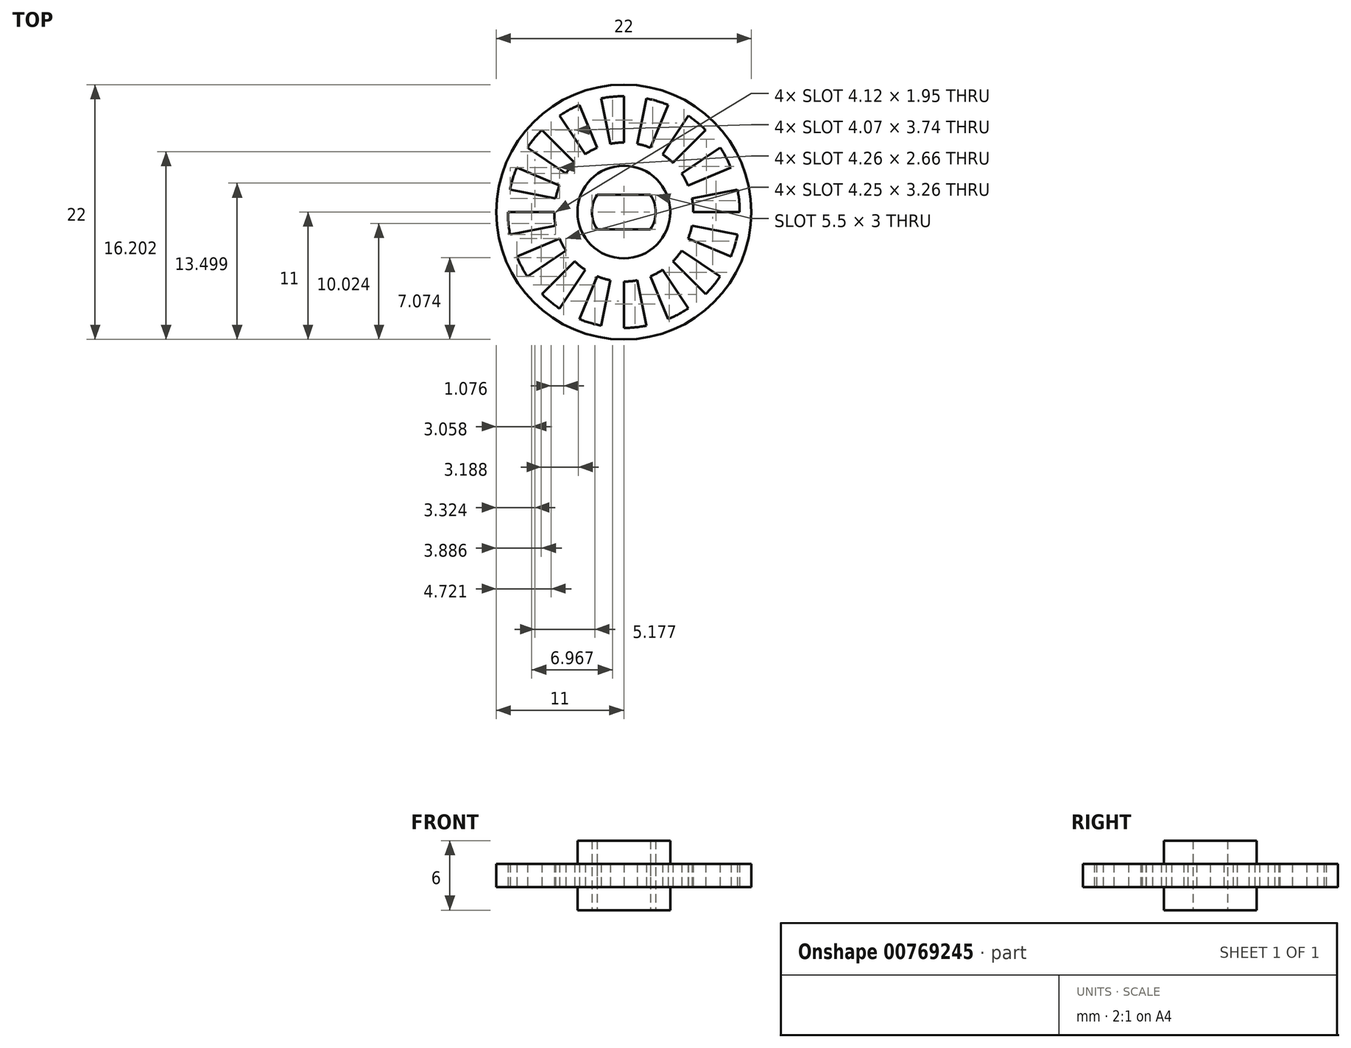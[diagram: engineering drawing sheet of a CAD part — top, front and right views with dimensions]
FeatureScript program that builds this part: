
annotation { "Feature Type Name" : "Feature", "Feature Type Description" : "" }
export const myFeature = defineFeature(function(context is Context, id is Id, definition is map)
    precondition{}
    {
        {
            var Q0;
            Q0=qCreatedBy(makeId("Top.planeOp"),FACE);
            var sketch = newSketch(context, id + "F0", { "sketchPlane" : qUnion([Q0])});
            skCircle(sketch, "E0", {"center": v(0, 0) * mm, "radius": 11 * mm});
            skArc(sketch, "E1", {"start": v(0, -10) * mm, "mid": v(0.98, -9.95) * mm, "end": v(1.95, -9.8) * mm});
            skArc(sketch, "E2", {"start": v(0, -6) * mm, "mid": v(0.59, -5.97) * mm, "end": v(1.17, -5.88) * mm});
            skLineSegment(sketch, "E3", {"start": v(0, -6) * mm, "end": v(0, -10) * mm});
            skLineSegment(sketch, "E4.1.0", {"start": v(1.17, -5.88) * mm, "end": v(1.95, -9.8) * mm});
            skLineSegment(sketch, "E4.2.0", {"start": v(2.3, -5.54) * mm, "end": v(3.83, -9.24) * mm});
            skLineSegment(sketch, "E4.3.0", {"start": v(3.33, -4.99) * mm, "end": v(5.56, -8.31) * mm});
            skLineSegment(sketch, "E4.4.0", {"start": v(4.24, -4.24) * mm, "end": v(7.07, -7.07) * mm});
            skLineSegment(sketch, "E4.5.0", {"start": v(4.99, -3.33) * mm, "end": v(8.31, -5.56) * mm});
            skLineSegment(sketch, "E4.6.0", {"start": v(5.54, -2.3) * mm, "end": v(9.24, -3.83) * mm});
            skLineSegment(sketch, "E4.7.0", {"start": v(5.88, -1.17) * mm, "end": v(9.8, -1.95) * mm});
            skLineSegment(sketch, "E4.8.0", {"start": v(6, 0) * mm, "end": v(10, 0) * mm});
            skLineSegment(sketch, "E4.9.0", {"start": v(5.88, 1.17) * mm, "end": v(9.8, 1.95) * mm});
            skLineSegment(sketch, "E4.10.0", {"start": v(5.54, 2.3) * mm, "end": v(9.24, 3.83) * mm});
            skLineSegment(sketch, "E4.11.0", {"start": v(4.99, 3.33) * mm, "end": v(8.31, 5.56) * mm});
            skLineSegment(sketch, "E4.12.0", {"start": v(4.24, 4.24) * mm, "end": v(7.07, 7.07) * mm});
            skLineSegment(sketch, "E4.13.0", {"start": v(3.33, 4.99) * mm, "end": v(5.56, 8.31) * mm});
            skLineSegment(sketch, "E4.14.0", {"start": v(2.3, 5.54) * mm, "end": v(3.83, 9.24) * mm});
            skLineSegment(sketch, "E4.15.0", {"start": v(1.17, 5.88) * mm, "end": v(1.95, 9.8) * mm});
            skLineSegment(sketch, "E4.16.0", {"start": v(0, 6) * mm, "end": v(0, 10) * mm});
            skLineSegment(sketch, "E4.17.0", {"start": v(-1.17, 5.88) * mm, "end": v(-1.95, 9.8) * mm});
            skLineSegment(sketch, "E4.18.0", {"start": v(-2.3, 5.54) * mm, "end": v(-3.83, 9.24) * mm});
            skLineSegment(sketch, "E4.19.0", {"start": v(-3.33, 4.99) * mm, "end": v(-5.56, 8.31) * mm});
            skLineSegment(sketch, "E4.20.0", {"start": v(-4.24, 4.24) * mm, "end": v(-7.07, 7.07) * mm});
            skLineSegment(sketch, "E4.21.0", {"start": v(-4.99, 3.33) * mm, "end": v(-8.31, 5.56) * mm});
            skLineSegment(sketch, "E4.22.0", {"start": v(-5.54, 2.3) * mm, "end": v(-9.24, 3.83) * mm});
            skLineSegment(sketch, "E4.23.0", {"start": v(-5.88, 1.17) * mm, "end": v(-9.8, 1.95) * mm});
            skLineSegment(sketch, "E4.24.0", {"start": v(-6, 0) * mm, "end": v(-10, 0) * mm});
            skLineSegment(sketch, "E4.25.0", {"start": v(-5.88, -1.17) * mm, "end": v(-9.8, -1.95) * mm});
            skLineSegment(sketch, "E4.26.0", {"start": v(-5.54, -2.3) * mm, "end": v(-9.24, -3.83) * mm});
            skLineSegment(sketch, "E4.27.0", {"start": v(-4.99, -3.33) * mm, "end": v(-8.31, -5.56) * mm});
            skLineSegment(sketch, "E4.28.0", {"start": v(-4.24, -4.24) * mm, "end": v(-7.07, -7.07) * mm});
            skLineSegment(sketch, "E4.29.0", {"start": v(-3.33, -4.99) * mm, "end": v(-5.56, -8.31) * mm});
            skLineSegment(sketch, "E4.30.0", {"start": v(-2.3, -5.54) * mm, "end": v(-3.83, -9.24) * mm});
            skLineSegment(sketch, "E4.31.0", {"start": v(-1.17, -5.88) * mm, "end": v(-1.95, -9.8) * mm});
            skArc(sketch, "E5.trimOffspring", {"start": v(-2.3, -5.54) * mm, "mid": v(-1.74, -5.74) * mm, "end": v(-1.17, -5.88) * mm});
            skArc(sketch, "E6.trimOffspring", {"start": v(-3.83, -9.24) * mm, "mid": v(-2.9, -9.57) * mm, "end": v(-1.95, -9.8) * mm});
            skArc(sketch, "E7.trimOffspring", {"start": v(-7.07, -7.07) * mm, "mid": v(-6.34, -7.73) * mm, "end": v(-5.56, -8.31) * mm});
            skArc(sketch, "E8.trimOffspring", {"start": v(-4.24, -4.24) * mm, "mid": v(-3.8, -4.64) * mm, "end": v(-3.33, -4.99) * mm});
            skArc(sketch, "E9.trimOffspring", {"start": v(-5.54, -2.3) * mm, "mid": v(-5.3, -2.83) * mm, "end": v(-4.99, -3.33) * mm});
            skArc(sketch, "E10.trimOffspring", {"start": v(-9.24, -3.83) * mm, "mid": v(-8.82, -4.71) * mm, "end": v(-8.31, -5.56) * mm});
            skArc(sketch, "E11.trimOffspring", {"start": v(-10, 0) * mm, "mid": v(-9.95, -0.98) * mm, "end": v(-9.8, -1.95) * mm});
            skArc(sketch, "E12.trimOffspring", {"start": v(-6, 0) * mm, "mid": v(-5.97, -0.59) * mm, "end": v(-5.88, -1.17) * mm});
            skArc(sketch, "E13.trimOffspring", {"start": v(-5.54, 2.3) * mm, "mid": v(-5.74, 1.74) * mm, "end": v(-5.88, 1.17) * mm});
            skArc(sketch, "E14.trimOffspring", {"start": v(-9.24, 3.83) * mm, "mid": v(-9.57, 2.9) * mm, "end": v(-9.8, 1.95) * mm});
            skArc(sketch, "E15.trimOffspring", {"start": v(-7.07, 7.07) * mm, "mid": v(-7.73, 6.34) * mm, "end": v(-8.31, 5.56) * mm});
            skArc(sketch, "E16.trimOffspring", {"start": v(-4.24, 4.24) * mm, "mid": v(-4.64, 3.8) * mm, "end": v(-4.99, 3.33) * mm});
            skArc(sketch, "E17.trimOffspring", {"start": v(-2.3, 5.54) * mm, "mid": v(-2.83, 5.3) * mm, "end": v(-3.33, 4.99) * mm});
            skArc(sketch, "E18.trimOffspring", {"start": v(-3.83, 9.24) * mm, "mid": v(-4.71, 8.82) * mm, "end": v(-5.56, 8.31) * mm});
            skArc(sketch, "E19.trimOffspring", {"start": v(0, 6) * mm, "mid": v(-0.59, 5.97) * mm, "end": v(-1.17, 5.88) * mm});
            skArc(sketch, "E20.trimOffspring", {"start": v(0, 10) * mm, "mid": v(-0.98, 9.95) * mm, "end": v(-1.95, 9.8) * mm});
            skArc(sketch, "E21.trimOffspring", {"start": v(3.83, 9.24) * mm, "mid": v(2.9, 9.57) * mm, "end": v(1.95, 9.8) * mm});
            skArc(sketch, "E22.trimOffspring", {"start": v(2.3, 5.54) * mm, "mid": v(1.74, 5.74) * mm, "end": v(1.17, 5.88) * mm});
            skArc(sketch, "E23.trimOffspring", {"start": v(4.24, 4.24) * mm, "mid": v(3.8, 4.64) * mm, "end": v(3.33, 4.99) * mm});
            skArc(sketch, "E24.trimOffspring", {"start": v(5.54, 2.3) * mm, "mid": v(5.3, 2.83) * mm, "end": v(4.99, 3.33) * mm});
            skArc(sketch, "E25.trimOffspring", {"start": v(6, 0) * mm, "mid": v(5.97, 0.59) * mm, "end": v(5.88, 1.17) * mm});
            skArc(sketch, "E26.trimOffspring", {"start": v(5.54, -2.3) * mm, "mid": v(5.74, -1.74) * mm, "end": v(5.88, -1.17) * mm});
            skArc(sketch, "E27.trimOffspring", {"start": v(4.24, -4.24) * mm, "mid": v(4.64, -3.8) * mm, "end": v(4.99, -3.33) * mm});
            skArc(sketch, "E28.trimOffspring", {"start": v(2.3, -5.54) * mm, "mid": v(2.83, -5.3) * mm, "end": v(3.33, -4.99) * mm});
            skArc(sketch, "E29.trimOffspring", {"start": v(3.83, -9.24) * mm, "mid": v(4.71, -8.82) * mm, "end": v(5.56, -8.31) * mm});
            skArc(sketch, "E30.trimOffspring", {"start": v(7.07, -7.07) * mm, "mid": v(7.73, -6.34) * mm, "end": v(8.31, -5.56) * mm});
            skArc(sketch, "E31.trimOffspring", {"start": v(9.24, -3.83) * mm, "mid": v(9.57, -2.9) * mm, "end": v(9.8, -1.95) * mm});
            skArc(sketch, "E32.trimOffspring", {"start": v(10, 0) * mm, "mid": v(9.95, 0.98) * mm, "end": v(9.8, 1.95) * mm});
            skArc(sketch, "E33.trimOffspring", {"start": v(9.24, 3.83) * mm, "mid": v(8.82, 4.71) * mm, "end": v(8.31, 5.56) * mm});
            skArc(sketch, "E34.trimOffspring", {"start": v(7.07, 7.07) * mm, "mid": v(6.34, 7.73) * mm, "end": v(5.56, 8.31) * mm});
            skCircle(sketch, "E35", {"center": v(0, 0) * mm, "radius": 4 * mm});
            skArc(sketch, "E36", {"start": v(-2.3, 1.5) * mm, "mid": v(-2.75, 0) * mm, "end": v(-2.3, -1.5) * mm});
            skLineSegment(sketch, "E37.bottom", {"start": v(2.3, 1.5) * mm, "end": v(-2.3, 1.5) * mm});
            skLineSegment(sketch, "E37.top", {"start": v(2.3, -1.5) * mm, "end": v(-2.3, -1.5) * mm});
            skArc(sketch, "E38.trimOffspring", {"start": v(2.3, -1.5) * mm, "mid": v(2.75, 0) * mm, "end": v(2.3, 1.5) * mm});
            skSolve(sketch);
        }
        {
            var Q0;
            Q0=makeQuery(id+"F0.imprint","IMPRINT",FACE,{"disambiguationData":[TD([[makeQuery(id+"F0.imprint","IMPRINT",EDGE,{"derivedFrom":sQuery(id+"F0.wireOp",EDGE,"E35")}),1.0]])]});
            extrude(context, id + "F1", {"entities" : qUnion([Q0]), "endBound" : BoundingType.SYMMETRIC, "depth" : 6 * mm, "offsetDistance" : 25 * mm});
        }
        {
            var Q0;
            Q0=makeQuery(id+"F0.imprint","IMPRINT",FACE,{"disambiguationData":[TD([[makeQuery(id+"F0.imprint","IMPRINT",EDGE,{"derivedFrom":sQuery(id+"F0.wireOp",EDGE,"E0")}),1.0]])]});
            extrude(context, id + "F2", {"entities" : qUnion([Q0]), "operationType" : NewBodyOperationType.ADD, "endBound" : BoundingType.SYMMETRIC, "depth" : 2 * mm, "offsetDistance" : 25 * mm});
        }
    });
